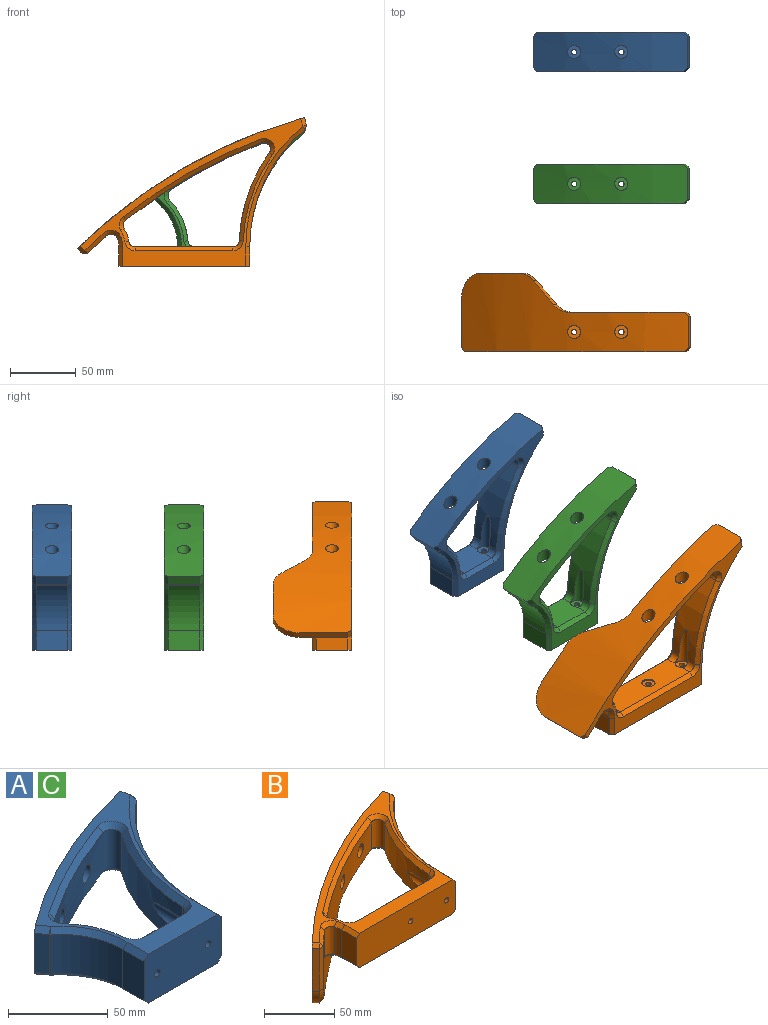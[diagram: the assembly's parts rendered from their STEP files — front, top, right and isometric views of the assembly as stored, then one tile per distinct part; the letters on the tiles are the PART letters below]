
ASSEMBLY  parts=3 mates=2
PART A: 62 faces, bbox 119.1x111.1x30 mm
  f0: cylinder r=120.16mm len=66.29mm, axis (0,0,-1), area 1524.4mm2, adj f1,f2,f10,f23,f32,f40
  f1: cylinder r=5mm len=8.33mm, axis (0,0,-1), area 55.5mm2, adj f0,f11,f23,f34
  f2: cylinder r=5mm len=8.33mm, axis (0,0,-1), area 55.5mm2, adj f0,f11,f23,f42
  f3: cylinder r=5mm len=8.23mm, axis (0,0,-1), area 53.8mm2, adj f5,f11,f25,f33
  f4: cylinder r=5mm len=8.23mm, axis (0,0,-1), area 53.8mm2, adj f5,f11,f25,f41
  f5: cylinder r=52.51mm len=31.13mm, axis (0,0,-1), area 722.3mm2, adj f3,f4,f12,f25,f31,f39
  f6: cylinder r=300mm len=117.82mm, axis (0,0,-1), area 3736.9mm2, adj f18,f19,f20,f21,f26,f27,f46,f49
  f7: cylinder r=292mm len=69.78mm, axis (0,0,-1), area 1708.3mm2, adj f10,f12,f26,f27,f28,f36
  f8: cylinder r=2.1mm len=14mm, axis (0,-1,0), area 184.7mm2, adj f15,f24
  f9: cylinder r=2.1mm len=14mm, axis (0,-1,0), area 184.7mm2, adj f15,f22
  f10: cylinder r=5mm len=24mm, axis (0,0,-1), area 304.9mm2, adj f0,f7,f30,f38
  f11: plane 29.32x24mm, normal (0,1,0), area 686.5mm2, adj f1,f2,f3,f4,f23,f25,f35,f43
  f12: cylinder r=5mm len=24mm, axis (0,0,-1), area 205.5mm2, adj f5,f7,f29,f37
  f13: cylinder r=44.51mm len=34.56mm, axis (0,0,-1), area 949.8mm2, adj f14,f45,f48,f52
  f14: plane 24x15mm, normal (-1,0,0), area 360mm2, adj f13,f15,f44,f50
  f15: plane 55x30mm, normal (0,-1,0), area 1604.3mm2, adj f8,f9,f14,f16,f20,f21,f44,f50
  f16: plane 24x15mm, normal (1,0,0), area 360mm2, adj f15,f17,f53,f60
  f17: cylinder r=112.16mm len=87.11mm, axis (0,0,-1), area 2393.8mm2, adj f16,f55,f58,f61
  f18: plane 24x5.98mm, normal (0.98,0.22,0), area 147.1mm2, adj f6,f54,f57,f58
  f19: plane 24x6.06mm, normal (-0.79,-0.61,0), area 183.4mm2, adj f6,f46,f48,f49
  f20: plane 113.83x110.4mm, normal (0,0,1), area 1704.3mm2, adj f6,f15,f36,f37,f38,f39,f40,f41
  f21: plane 113.83x110.4mm, normal (0,0,-1), area 1704.3mm2, adj f6,f15,f28,f29,f30,f31,f32,f33
  f22: plane 10x10mm, normal (0,1,0), area 64.7mm2, adj f9,f23
  f23: cylinder r=5mm len=29.8mm, axis (0,-1,0), area 323.4mm2, adj f0,f1,f2,f11,f22
  f24: plane 10x10mm, normal (0,1,0), area 64.7mm2, adj f8,f25
  f25: cylinder r=5mm len=19.85mm, axis (0,-1,0), area 226mm2, adj f3,f4,f5,f11,f24
  f26: cylinder r=5mm len=15.29mm, axis (0,-1,0), area 292.7mm2, adj f6,f7
  f27: cylinder r=5mm len=12.94mm, axis (0,-1,0), area 273mm2, adj f6,f7
  f28: cone r=295mm half-angle=45deg, axis (0,0,-1), area 335mm2, adj f7,f21,f29,f30
  f29: cone r=8mm half-angle=45deg, axis (0,0,-1), area 47.2mm2, adj f12,f21,f28,f31
  f30: cone r=8mm half-angle=45deg, axis (0,0,-1), area 70.1mm2, adj f10,f21,f28,f32
  f31: cone r=52.51mm half-angle=45deg, axis (0,0,1), area 142.9mm2, adj f5,f21,f29,f33
  f32: cone r=120.16mm half-angle=45deg, axis (0,0,1), area 298.6mm2, adj f0,f21,f30,f34
  f33: cone r=8mm half-angle=45deg, axis (0,0,-1), area 40.9mm2, adj f3,f21,f31,f35
  f34: cone r=8mm half-angle=45deg, axis (0,0,-1), area 42.2mm2, adj f1,f21,f32,f35
  f35: plane 29.32x3mm, normal (0,0.71,-0.71), area 124.4mm2, adj f11,f21,f33,f34
  f36: cone r=292mm half-angle=45deg, axis (0,0,1), area 335mm2, adj f7,f20,f37,f38
  f37: cone r=5mm half-angle=45deg, axis (0,0,1), area 47.2mm2, adj f12,f20,f36,f39
  f38: cone r=5mm half-angle=45deg, axis (0,0,1), area 70.1mm2, adj f10,f20,f36,f40
  f39: cone r=49.51mm half-angle=45deg, axis (0,0,-1), area 142.9mm2, adj f5,f20,f37,f41
  f40: cone r=117.16mm half-angle=45deg, axis (0,0,-1), area 298.6mm2, adj f0,f20,f38,f42
  f41: cone r=5mm half-angle=45deg, axis (0,0,1), area 40.9mm2, adj f4,f20,f39,f43
  f42: cone r=5mm half-angle=45deg, axis (0,0,1), area 42.2mm2, adj f2,f20,f40,f43
  f43: plane 29.32x3mm, normal (0,0.71,0.71), area 124.4mm2, adj f11,f20,f41,f42
  f44: plane 15x3mm, normal (-0.71,0,-0.71), area 63.6mm2, adj f14,f15,f21,f45
  f45: cone r=47.51mm half-angle=45deg, axis (0,0,-1), area 173.6mm2, adj f13,f21,f44,f47
  f46: plane 7.88x7.03mm, normal (-0.56,-0.43,-0.71), area 32.4mm2, adj f6,f19,f21,f47
  f47: plane 3x2.38mm, normal (-0.51,-0.49,-0.7), area 1.5mm2, adj f45,f46,f48
  f48: plane 24x0.5mm, normal (-0.72,-0.7,0), area 16.8mm2, adj f13,f19,f47,f51
  f49: plane 7.88x7.03mm, normal (-0.56,-0.43,0.71), area 32.4mm2, adj f6,f19,f20,f51
  f50: plane 15x3mm, normal (-0.71,0,0.71), area 63.6mm2, adj f14,f15,f20,f52
  f51: plane 3x2.38mm, normal (-0.51,-0.49,0.7), area 1.5mm2, adj f48,f49,f52
  f52: cone r=44.51mm half-angle=45deg, axis (0,0,1), area 173.6mm2, adj f13,f20,f50,f51
  f53: plane 15x3mm, normal (0.71,0,-0.71), area 63.6mm2, adj f15,f16,f21,f55
  f54: plane 6.63x4.25mm, normal (0.69,0.15,-0.71), area 26mm2, adj f6,f18,f21,f56
  f55: cone r=115.16mm half-angle=45deg, axis (0,0,-1), area 428.8mm2, adj f17,f21,f53,f56
  f56: plane 3x2.98mm, normal (0.72,-0.25,-0.65), area 6.2mm2, adj f54,f55,f58
  f57: plane 6.63x4.25mm, normal (0.69,0.15,0.71), area 26mm2, adj f6,f18,f20,f59
  f58: plane 24x2.98mm, normal (0.94,-0.33,0), area 75.7mm2, adj f17,f18,f56,f59
  f59: plane 3x2.98mm, normal (0.72,-0.25,0.65), area 6.2mm2, adj f57,f58,f61
  f60: plane 15x3mm, normal (0.71,0,0.71), area 63.6mm2, adj f15,f16,f20,f61
  f61: cone r=112.16mm half-angle=45deg, axis (0,0,1), area 428.8mm2, adj f17,f20,f59,f60
PART B: 73 faces, bbox 174.8x113.6x60 mm
  f0: plane 144.77x112.77mm, normal (0,0,-1), area 2041.7mm2, adj f1,f8,f11,f31,f33,f34,f35,f36
  f1: cylinder r=400mm len=173.21mm, axis (0,0,-1), area 8192.2mm2, adj f0,f7,f19,f20,f25,f26,f27,f29
  f2: cylinder r=124.05mm len=67.06mm, axis (0,0,-1), area 1534.8mm2, adj f3,f4,f15,f22,f38,f56
  f3: cylinder r=5mm len=8.34mm, axis (0,0,-1), area 59.7mm2, adj f2,f16,f22,f37
  f4: cylinder r=5mm len=8.34mm, axis (0,0,-1), area 59.7mm2, adj f2,f16,f22,f54
  f5: cylinder r=2.1mm len=14mm, axis (0,-1,0), area 184.7mm2, adj f11,f23
  f6: cylinder r=2.1mm len=14mm, axis (0,-1,0), area 184.7mm2, adj f11,f21
  f7: plane 37x3.58mm, normal (-0.71,-0.7,0), area 185.4mm2, adj f1,f32,f47,f52
  f8: cylinder r=392mm len=132.82mm, axis (0,0,-1), area 5323.5mm2, adj f0,f14,f15,f25,f26,f28,f33,f40
  f9: cylinder r=19.1mm len=24mm, axis (0,0,-1), area 154.3mm2, adj f10,f28,f43,f62
  f10: plane 24x15mm, normal (-1,0,0), area 360mm2, adj f9,f11,f41,f61
  f11: plane 100x30mm, normal (0,-1,0), area 2954.3mm2, adj f0,f5,f6,f10,f12,f20,f41,f61
  f12: plane 24x15mm, normal (1,0,0), area 360mm2, adj f11,f13,f64,f72
  f13: cylinder r=116.05mm len=89.65mm, axis (0,0,-1), area 2458.8mm2, adj f12,f66,f69,f71
  f14: cylinder r=5mm len=24mm, axis (0,0,-1), area 172.9mm2, adj f8,f18,f33,f59
  f15: cylinder r=5mm len=24mm, axis (0,0,-1), area 306.4mm2, adj f2,f8,f39,f58
  f16: plane 74.49x24mm, normal (0,1,0), area 1701.1mm2, adj f3,f4,f17,f22,f24,f36,f53
  f17: cylinder r=5mm len=24mm, axis (0,0,-1), area 169.7mm2, adj f16,f18,f35,f55
  f18: cylinder r=27.1mm len=24mm, axis (0,0,-1), area 249.3mm2, adj f14,f17,f34,f57
  f19: plane 24x5.81mm, normal (0.96,0.27,0), area 144.7mm2, adj f1,f65,f68,f69
  f20: plane 169.78x112.77mm, normal (0,0,1), area 2571.5mm2, adj f1,f11,f41,f43,f45,f47,f48,f53
  f21: plane 10x10mm, normal (0,1,0), area 64.7mm2, adj f6,f22
  f22: cylinder r=5mm len=30.27mm, axis (0,-1,0), area 342.8mm2, adj f2,f3,f4,f16,f21
  f23: plane 10x10mm, normal (0,1,0), area 64.7mm2, adj f5,f24
  f24: cylinder r=5mm len=10mm, axis (0,-1,0), area 31.4mm2, adj f16,f23
  f25: cylinder r=5mm len=10mm, axis (0,-1,0), area 274.2mm2, adj f1,f8
  f26: cylinder r=5mm len=10mm, axis (0,-1,0), area 288.4mm2, adj f1,f8
  f27: plane 31.35x26.73mm, normal (0,0,-1), area 181.6mm2, adj f1,f30,f32,f49
  f28: cylinder r=5mm len=24mm, axis (0,0,1), area 234.2mm2, adj f8,f9,f45,f63
  f29: plane 18.29x18.04mm, normal (0.59,0.39,-0.71), area 129.4mm2, adj f1,f30,f31,f44
  f30: cylinder r=20mm len=14.9mm, axis (-0.54,0.84,0), area 79mm2, adj f1,f27,f29,f46
  f31: cylinder r=20mm len=14.9mm, axis (-0.54,0.84,0), area 78.3mm2, adj f0,f1,f29,f42
  f32: cylinder r=20mm len=20mm, axis (0.7,-0.71,0), area 157.4mm2, adj f1,f7,f27,f51
  f33: cone r=8mm half-angle=45deg, axis (0,0,-1), area 26.3mm2, adj f0,f8,f14,f34
  f34: cone r=27.1mm half-angle=45deg, axis (0,0,1), area 41.6mm2, adj f0,f18,f33,f35
  f35: cone r=8mm half-angle=45deg, axis (0,0,-1), area 39mm2, adj f0,f17,f34,f36
  f36: plane 74.49x3mm, normal (0,0.71,-0.71), area 316mm2, adj f0,f16,f35,f37
  f37: cone r=8mm half-angle=45deg, axis (0,0,-1), area 42.2mm2, adj f0,f3,f36,f38
  f38: cone r=124.05mm half-angle=45deg, axis (0,0,1), area 301.1mm2, adj f0,f2,f37,f39
  f39: cone r=8mm half-angle=45deg, axis (0,0,-1), area 70.4mm2, adj f0,f15,f38,f40
  f40: cone r=395mm half-angle=45deg, axis (0,0,-1), area 254.7mm2, adj f0,f8,f39,f42
  f41: plane 15x3mm, normal (-0.71,0,0.71), area 63.6mm2, adj f10,f11,f20,f43
  f42: bspline ~13.87x10.88mm, area 71.9mm2, adj f8,f31,f40,f44
  f43: cone r=19.1mm half-angle=45deg, axis (0,0,1), area 29.4mm2, adj f9,f20,f41,f45
  f44: bspline ~20.41x15.36mm, area 109.3mm2, adj f8,f29,f42,f46
  f45: cone r=8mm half-angle=45deg, axis (0,0,1), area 53.8mm2, adj f20,f28,f43,f48
  f46: bspline ~11.57x10.56mm, area 61.1mm2, adj f8,f30,f44,f49
  f47: plane 5.67x5.65mm, normal (-0.5,-0.5,0.71), area 21.2mm2, adj f1,f7,f20,f50
  f48: cone r=392mm half-angle=45deg, axis (0,0,1), area 84.8mm2, adj f8,f20,f45,f50
  f49: cone r=395mm half-angle=45deg, axis (0,0,-1), area 151.4mm2, adj f8,f27,f46,f51
  f50: plane 4.23x3mm, normal (-0.01,-0.82,0.58), area 7.8mm2, adj f47,f48,f52
  f51: bspline ~20x16.61mm, area 122.4mm2, adj f8,f32,f49,f52
  f52: plane 37x4.23mm, normal (-0.01,-1,0), area 156.4mm2, adj f7,f8,f50,f51
  f53: plane 74.49x3mm, normal (0,0.71,0.71), area 316mm2, adj f16,f20,f54,f55
  f54: cone r=5mm half-angle=45deg, axis (0,0,1), area 42.2mm2, adj f4,f20,f53,f56
  f55: cone r=5mm half-angle=45deg, axis (0,0,1), area 39mm2, adj f17,f20,f53,f57
  f56: cone r=121.05mm half-angle=45deg, axis (0,0,-1), area 301.1mm2, adj f2,f20,f54,f58
  f57: cone r=24.1mm half-angle=45deg, axis (0,0,-1), area 41.6mm2, adj f18,f20,f55,f59
  f58: cone r=5mm half-angle=45deg, axis (0,0,1), area 70.4mm2, adj f15,f20,f56,f60
  f59: cone r=5mm half-angle=45deg, axis (0,0,1), area 39.7mm2, adj f14,f20,f57,f60
  f60: cone r=392mm half-angle=45deg, axis (0,0,1), area 510.3mm2, adj f8,f20,f58,f59
  f61: plane 15x3mm, normal (-0.71,0,-0.71), area 63.6mm2, adj f0,f10,f11,f62
  f62: cone r=22.1mm half-angle=45deg, axis (0,0,-1), area 29.4mm2, adj f0,f9,f61,f63
  f63: cone r=8mm half-angle=45deg, axis (0,0,-1), area 40.4mm2, adj f0,f8,f28,f62
  f64: plane 15x3mm, normal (0.71,0,-0.71), area 63.6mm2, adj f0,f11,f12,f66
  f65: plane 6.61x4.5mm, normal (0.68,0.19,-0.71), area 25.6mm2, adj f0,f1,f19,f67
  f66: cone r=119.05mm half-angle=45deg, axis (0,0,-1), area 440.3mm2, adj f0,f13,f64,f67
  f67: plane 3.12x3mm, normal (0.73,-0.23,-0.64), area 6.4mm2, adj f65,f66,f69
  f68: plane 6.61x4.5mm, normal (0.68,0.19,0.71), area 25.6mm2, adj f1,f19,f20,f70
  f69: plane 24x3.12mm, normal (0.95,-0.3,0), area 78.5mm2, adj f13,f19,f67,f70
  f70: plane 3.12x3mm, normal (0.73,-0.23,0.64), area 6.4mm2, adj f68,f69,f71
  f71: cone r=116.05mm half-angle=45deg, axis (0,0,1), area 440.3mm2, adj f13,f20,f70,f72
  f72: plane 15x3mm, normal (0.71,0,0.71), area 63.6mm2, adj f11,f12,f20,f71
PART C: same geometry as A
PLACE A rot(axis=(1,0,0),90deg) t=(64.53,15,0)mm
PLACE B rot(axis=(1,0,0),90deg) t=(64.53,-198.67,0)mm
PLACE C rot(axis=(1,0,0),90deg) t=(64.53,-85.63,0)mm
MATE planar B.f12 <-> C.f16  axis (1,0,0) through (119.53,-213.67,7.5)mm
MATE planar B.f12 <-> A.f16  axis (1,0,0) through (119.53,-213.67,7.5)mm
